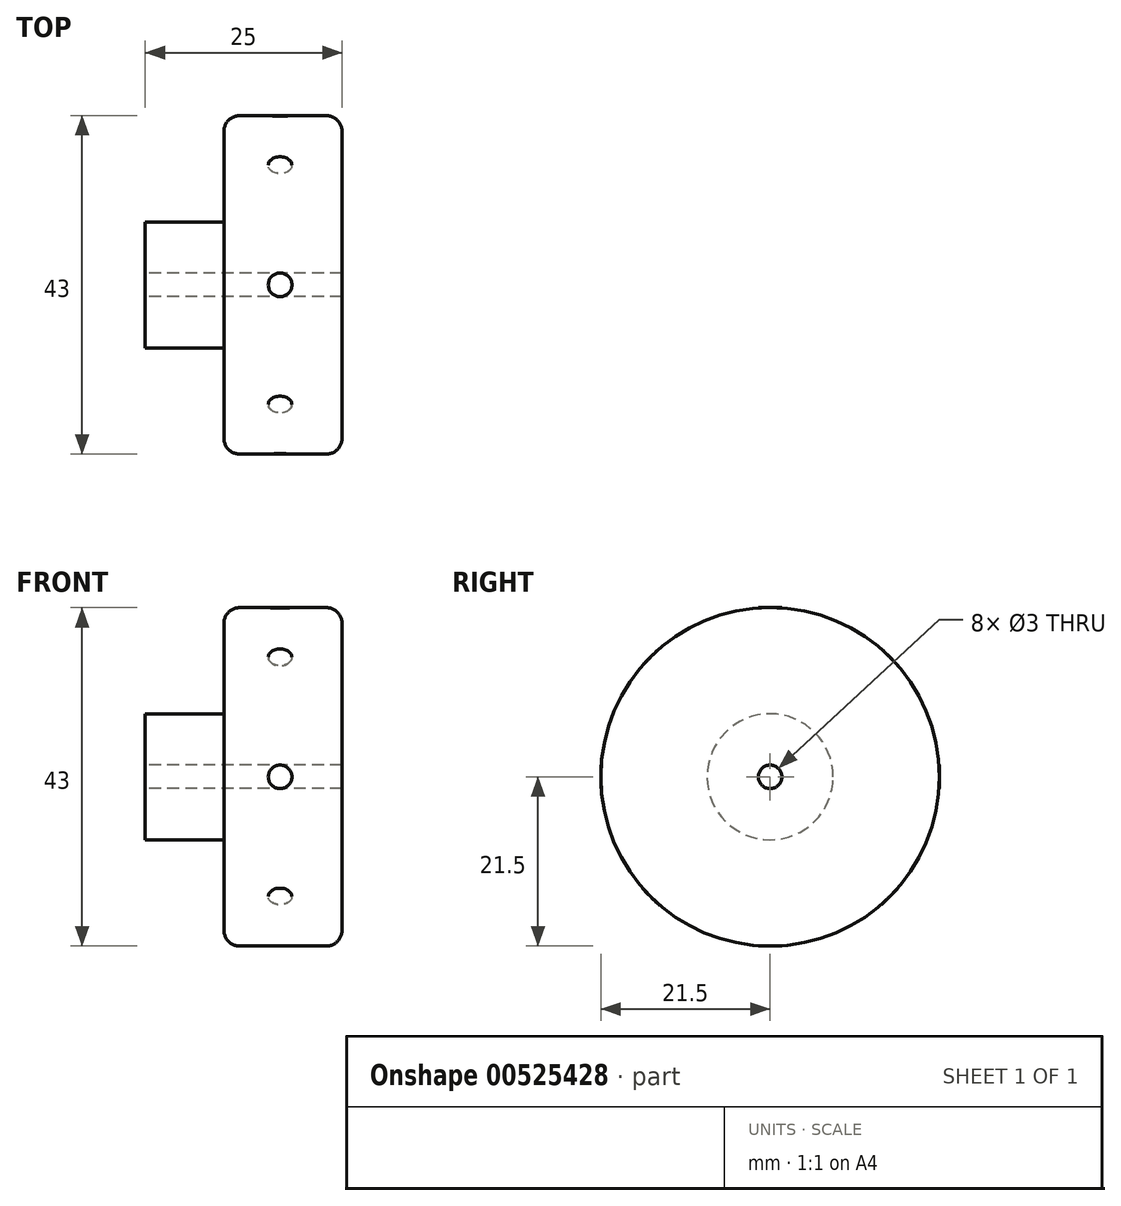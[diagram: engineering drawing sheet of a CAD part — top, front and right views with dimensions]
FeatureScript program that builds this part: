
annotation { "Feature Type Name" : "Feature", "Feature Type Description" : "" }
export const myFeature = defineFeature(function(context is Context, id is Id, definition is map)
    precondition{}
    {
        {
            var Q0;
            Q0=qCreatedBy(makeId("Front.planeOp"),FACE);
            var sketch = newSketch(context, id + "F0", { "sketchPlane" : qUnion([Q0])});
            skLineSegment(sketch, "E0", {"start": v(25, 21.5) * mm, "end": v(10, 21.5) * mm});
            skLineSegment(sketch, "E1", {"start": v(10, 21.5) * mm, "end": v(10, 8) * mm});
            skLineSegment(sketch, "E2", {"start": v(10, 8) * mm, "end": v(0, 8) * mm});
            skLineSegment(sketch, "E3", {"start": v(25, 21.5) * mm, "end": v(25, 1.5) * mm});
            skLineSegment(sketch, "E4", {"start": v(25, 1.5) * mm, "end": v(0, 1.5) * mm});
            skLineSegment(sketch, "E5", {"start": v(0, 1.5) * mm, "end": v(0, 8) * mm});
            skLineSegment(sketch, "E6", {"start": v(0, 47.38) * mm, "end": v(0, -45.58) * mm, "construction": true});
            skLineSegment(sketch, "E7", {"start": v(-43.78, 0) * mm, "end": v(41.41, 0) * mm, "construction": true});
            skSolve(sketch);
        }
        {
            var Q0;
            Q0 = qSketchRegion(id + "F0", true);
            var Q1;
            Q1=sQuery(id+"F0.wireOp",EDGE,"E7");
            revolve(context, id + "F1", {"entities" : qUnion([Q0]), "axis" : qUnion([Q1]), "revolveType" : RevolveType.FULL});
        }
        {
            var Q0;
            Q0=qCreatedBy(makeId("Front.planeOp"),FACE);
            cPlane(context, id + "F2", {"entities" : qUnion([Q0]), "cplaneType" : CPlaneType.OFFSET, "offset" : 21.5 * mm, "width" : 150 * mm, "height" : 150 * mm});
        }
        {
            var Q0;
            Q0=makeQuery(id+"F1.opRevolve","SWEPT_EDGE",EDGE,{"disambiguationData":[OSD([sQuery(id+"F0.wireOp",EDGE,"E0"),sQuery(id+"F0.wireOp",EDGE,"E1")])]});
            var Q1;
            Q1=makeQuery(id+"F1.opRevolve","SWEPT_EDGE",EDGE,{"disambiguationData":[OSD([sQuery(id+"F0.wireOp",EDGE,"E0"),sQuery(id+"F0.wireOp",EDGE,"E3")])]});
            fillet(context, id + "F3", {"entities" : qUnion([Q0, Q1]), "radius" : 2 * mm, "tangentPropagation" : true, "allowEdgeOverflow" : false});
        }
        {
            var Q0;
            Q0=qCreatedBy(id+"F2.planeOp",FACE);
            var sketch = newSketch(context, id + "F4", { "sketchPlane" : qUnion([Q0])});
            skLineSegment(sketch, "E8", {"start": v(0, 0) * mm, "end": v(17.14, 0) * mm});
            skCircle(sketch, "E9", {"center": v(17.14, 0) * mm, "radius": 1.5 * mm});
            skSolve(sketch);
        }
        {
            var Q0;
            Q0=makeQuery(id+"F4.imprint","IMPRINT",FACE,{"disambiguationData":[TD([[makeQuery(id+"F4.imprint","IMPRINT",EDGE,{"derivedFrom":sQuery(id+"F4.wireOp",EDGE,"E9")}),1.0]])]});
            extrude(context, id + "F5", {"entities" : qUnion([Q0]), "operationType" : NewBodyOperationType.ADD, "oppositeDirection" : true, "depth" : 15 * mm, "offsetDistance" : 25 * mm});
        }
        {
            var Q0;
            Q0=makeQuery(id+"F1.opRevolve","SWEPT_BODY",BODY,{"disambiguationData":[OSD([sQuery(id+"F0.wireOp",EDGE,"E0"),sQuery(id+"F0.wireOp",EDGE,"E1"),sQuery(id+"F0.wireOp",EDGE,"E2"),sQuery(id+"F0.wireOp",EDGE,"E3"),sQuery(id+"F0.wireOp",EDGE,"E4"),sQuery(id+"F0.wireOp",EDGE,"E5")])]});
            var Q1;
            Q1=makeQuery(id+"F1.opRevolve","SWEPT_FACE",FACE,{"disambiguationData":[OSD([sQuery(id+"F0.wireOp",EDGE,"E0")])]});
            circularPattern(context, id + "F6", {"entities" : qUnion([Q0]), "axis" : qUnion([Q1]), "angle" : 360 * degree, "instanceCount" : 8, "equalSpace" : true});
        }
    });
